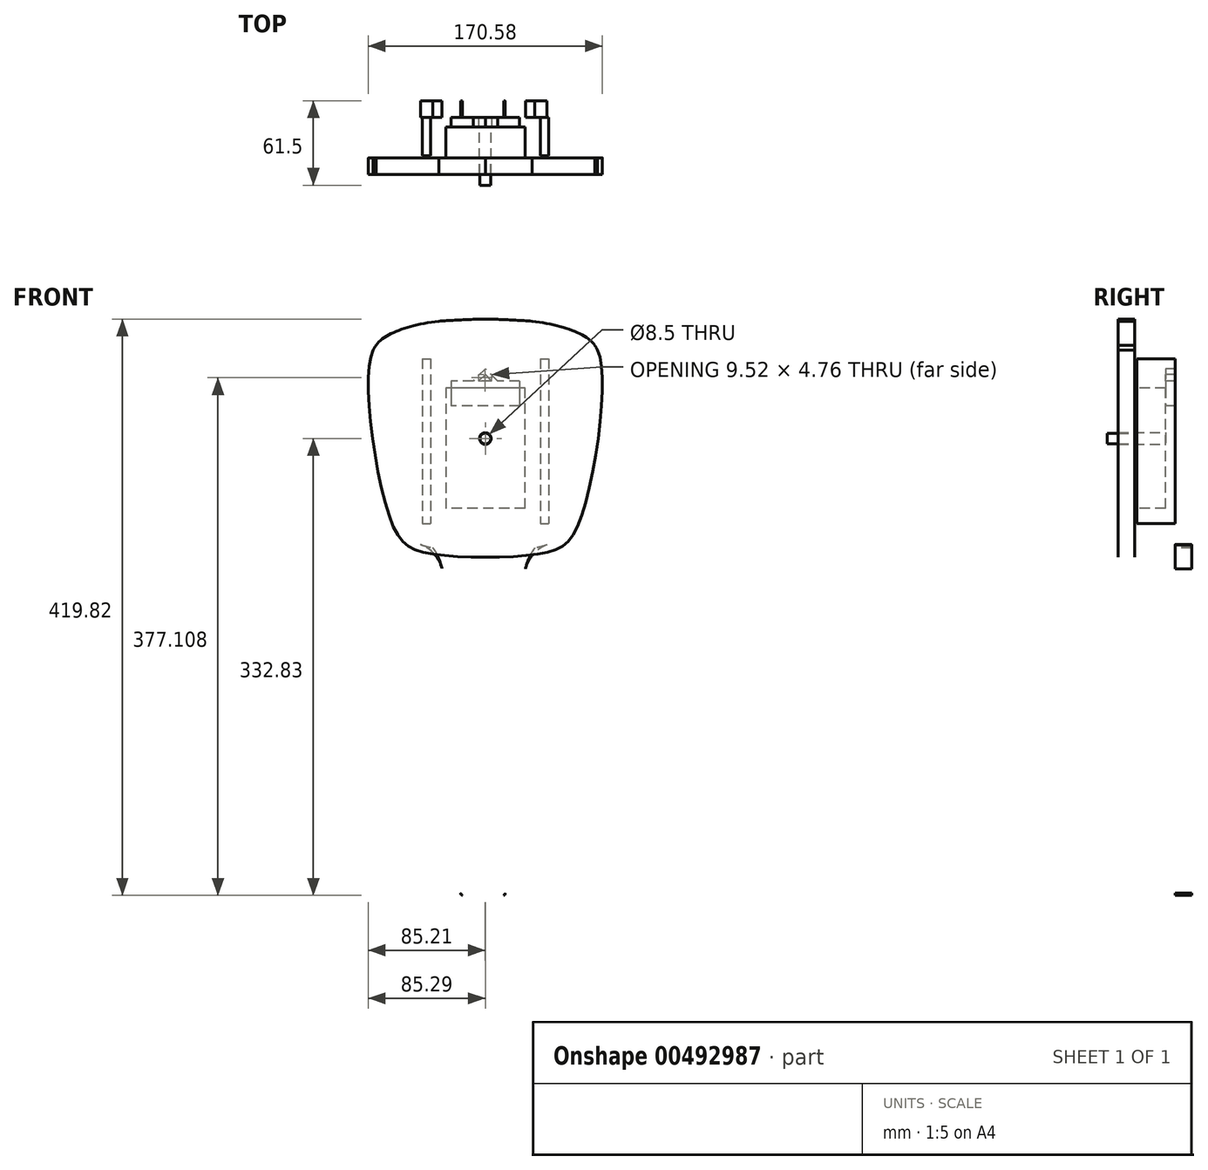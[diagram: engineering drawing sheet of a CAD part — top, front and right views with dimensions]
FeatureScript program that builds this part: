
annotation { "Feature Type Name" : "Feature", "Feature Type Description" : "" }
export const myFeature = defineFeature(function(context is Context, id is Id, definition is map)
    precondition{}
    {
        {
            var Q0;
            Q0=qCreatedBy(makeId("Front.planeOp"),FACE);
            var sketch = newSketch(context, id + "F0", { "sketchPlane" : qUnion([Q0])});
            skLineSegment(sketch, "E0", {"start": v(0, 92.19) * mm, "end": v(0, -94.4) * mm, "construction": true});
            skFitSpline(sketch, "E1", {"points": [v(-34.18, 85.43) * mm, v(-82.75, 62.27) * mm, v(-69.15, -63.66) * mm, v(-45.13, -83.34) * mm, v(40.74, -83.8) * mm, v(67.58, -62.92) * mm, v(84.8, 51.66) * mm, v(72.84, 74.07) * mm, v(35.33, 85.27) * mm, v(-34.18, 85.43) * mm]});
            skFitSpline(sketch, "E2.MirrorCS", {"points": [v(34.18, 85.43) * mm, v(82.75, 62.27) * mm, v(69.15, -63.66) * mm, v(45.13, -83.34) * mm, v(-40.74, -83.8) * mm, v(-67.58, -62.92) * mm, v(-84.8, 51.66) * mm, v(-72.84, 74.07) * mm, v(-35.33, 85.27) * mm, v(34.18, 85.43) * mm]});
            skSolve(sketch);
        }
        {
            var Q0;
            Q0=makeQuery(id+"F0.imprint","IMPRINT",FACE,{"disambiguationData":[TD([[makeQuery(id+"F0.imprint","IMPRINT",EDGE,{"derivedFrom":sQuery(id+"F0.wireOp",EDGE,"E1")}),1.0]])]});
            extrude(context, id + "F1", {"entities" : qUnion([Q0]), "depth" : 12 * mm});
        }
        {
            var Q0;
            Q0=makeQuery(id+"F1.opExtrude","CAP_FACE",FACE,{"disambiguationData":[OSD([sQuery(id+"F0.wireOp",EDGE,"E1"),sQuery(id+"F0.wireOp",EDGE,"E2.MirrorCS")])],"isStart":true});
            var sketch = newSketch(context, id + "F2", { "sketchPlane" : qUnion([Q0])});
            skCircle(sketch, "E3", {"center": v(0, 0) * mm, "radius": 4.25 * mm});
            skSolve(sketch);
        }
        {
            var Q0;
            Q0=makeQuery(id+"F2.imprint","IMPRINT",FACE,{"disambiguationData":[TD([[makeQuery(id+"F2.imprint","IMPRINT",EDGE,{"derivedFrom":sQuery(id+"F2.wireOp",EDGE,"E3")}),1.0]])]});
            extrude(context, id + "F3", {"entities" : qUnion([Q0]), "operationType" : NewBodyOperationType.REMOVE, "oppositeDirection" : true, "depth" : 25 * mm});
        }
        {
            var Q0;
            Q0=makeQuery(id+"F1.opExtrude","CAP_FACE",FACE,{"disambiguationData":[OSD([sQuery(id+"F0.wireOp",EDGE,"E1"),sQuery(id+"F0.wireOp",EDGE,"E2.MirrorCS")])],"isStart":false});
            var sketch = newSketch(context, id + "F4", { "sketchPlane" : qUnion([Q0])});
            skCircle(sketch, "E4", {"center": v(0, 0) * mm, "radius": 3.9 * mm});
            skSolve(sketch);
        }
        {
            var Q0;
            Q0=makeQuery(id+"F4.imprint","IMPRINT",FACE,{"disambiguationData":[TD([[makeQuery(id+"F4.imprint","IMPRINT",EDGE,{"derivedFrom":sQuery(id+"F4.wireOp",EDGE,"E4")}),1.0]])]});
            var Q1;
            Q1=sQuery(id+"F4.wireOp",EDGE,"E4");
            extrude(context, id + "F5", {"entities" : qUnion([Q0]), "surfaceEntities" : qUnion([Q1]), "depth" : 8 * mm, "hasSecondDirection" : true, "secondDirectionOppositeDirection" : true, "secondDirectionDepth" : 12 * mm});
        }
        {
            var Q0;
            Q0=makeQuery(id+"F1.opExtrude","CAP_FACE",FACE,{"disambiguationData":[OSD([sQuery(id+"F0.wireOp",EDGE,"E1"),sQuery(id+"F0.wireOp",EDGE,"E2.MirrorCS")])],"isStart":true});
            var sketch = newSketch(context, id + "F6", { "sketchPlane" : qUnion([Q0])});
            skLineSegment(sketch, "E5", {"start": v(-28.9, 36.9) * mm, "end": v(28.9, 36.9) * mm});
            skLineSegment(sketch, "E6", {"start": v(-28.9, -50.9) * mm, "end": v(28.9, -50.9) * mm});
            skLineSegment(sketch, "E7", {"start": v(-28.9, -50.9) * mm, "end": v(-28.9, 36.9) * mm});
            skLineSegment(sketch, "E8", {"start": v(28.9, 36.9) * mm, "end": v(28.9, -50.9) * mm});
            skSolve(sketch);
        }
        {
            var Q0;
            Q0=makeQuery(id+"F6.imprint","IMPRINT",FACE,{"disambiguationData":[TD([[makeQuery(id+"F6.imprint","IMPRINT",EDGE,{"derivedFrom":sQuery(id+"F6.wireOp",EDGE,"E5")}),-1.0]])]});
            extrude(context, id + "F7", {"entities" : qUnion([Q0]), "operationType" : NewBodyOperationType.ADD, "depth" : 22.5 * mm});
        }
        {
            var Q0;
            Q0=makeQuery(id+"F7.opExtrude","CAP_FACE",FACE,{"disambiguationData":[OSD([sQuery(id+"F2.wireOp",EDGE,"E3"),sQuery(id+"F6.wireOp",EDGE,"E5"),sQuery(id+"F6.wireOp",EDGE,"E6"),sQuery(id+"F6.wireOp",EDGE,"E7"),sQuery(id+"F6.wireOp",EDGE,"E8")])],"isStart":false});
            var sketch = newSketch(context, id + "F8", { "sketchPlane" : qUnion([Q0])});
            skLineSegment(sketch, "E9.bottom", {"start": v(-25, 41.9) * mm, "end": v(-8.85, 41.9) * mm});
            skLineSegment(sketch, "E9.top", {"start": v(-25, 23.9) * mm, "end": v(25, 23.9) * mm});
            skLineSegment(sketch, "E9.left", {"start": v(-25, 41.9) * mm, "end": v(-25, 23.9) * mm});
            skLineSegment(sketch, "E9.right", {"start": v(25, 41.9) * mm, "end": v(25, 23.9) * mm});
            skLineSegment(sketch, "E10", {"start": v(-8.85, 41.9) * mm, "end": v(0, 50.9) * mm});
            skPoint(sketch, "E10.endSnap0", {"position": v(0, 41.9) * mm});
            skLineSegment(sketch, "E11", {"start": v(0, 50.9) * mm, "end": v(8.85, 41.9) * mm});
            skLineSegment(sketch, "E12", {"start": v(-4.68, 41.9) * mm, "end": v(0, 46.66) * mm});
            skLineSegment(sketch, "E13", {"start": v(0, 46.66) * mm, "end": v(4.84, 41.9) * mm});
            skLineSegment(sketch, "E14.trimOffspring", {"start": v(-4.68, 41.9) * mm, "end": v(4.84, 41.9) * mm});
            skLineSegment(sketch, "E15.trimOffspring", {"start": v(8.85, 41.9) * mm, "end": v(25, 41.9) * mm});
            skSolve(sketch);
        }
        {
            var Q0;
            Q0 = qSketchRegion(id + "F8", true);
            extrude(context, id + "F9", {"entities" : qUnion([Q0]), "operationType" : NewBodyOperationType.ADD, "depth" : 7 * mm});
        }
        {
            var Q0;
            Q0=makeQuery(id+"F9.opExtrude","CAP_FACE",FACE,{"disambiguationData":[OSD([sQuery(id+"F8.wireOp",EDGE,"E9.bottom"),sQuery(id+"F8.wireOp",EDGE,"E9.top"),sQuery(id+"F8.wireOp",EDGE,"E9.left"),sQuery(id+"F8.wireOp",EDGE,"E9.right"),sQuery(id+"F8.wireOp",EDGE,"E10"),sQuery(id+"F8.wireOp",EDGE,"E11"),sQuery(id+"F8.wireOp",EDGE,"E12"),sQuery(id+"F8.wireOp",EDGE,"E13"),sQuery(id+"F8.wireOp",EDGE,"E14.trimOffspring"),sQuery(id+"F8.wireOp",EDGE,"E15.trimOffspring")])],"isStart":false});
            var sketch = newSketch(context, id + "F10", { "sketchPlane" : qUnion([Q0])});
            skLineSegment(sketch, "E16", {"start": v(0.68, 132.03) * mm, "end": v(1.75, -338.07) * mm, "construction": true});
            skFitSpline(sketch, "E17.MirrorCS", {"points": [v(-36.07, -79.67) * mm, v(-38.31, -176.64) * mm], "startDerivative": vector(50.2, -64.86) * mm, "endDerivative": vector(-28.7, -66.43) * mm});
            skFitSpline(sketch, "E18.MirrorCS", {"points": [v(-39.85, -215.04) * mm, v(-38.31, -176.64) * mm], "startDerivative": vector(31.7, 21.38) * mm, "endDerivative": vector(-33.38, 61.08) * mm});
            skFitSpline(sketch, "E19.MirrorCS", {"points": [v(-36.04, -307.45) * mm, v(-49.96, -244.84) * mm, v(-39.85, -215.04) * mm], "startDerivative": vector(-116.27, 61.82) * mm, "endDerivative": vector(-62.13, 120.79) * mm});
            skFitSpline(sketch, "E20.MirrorCS", {"points": [v(-14.34, -332.34) * mm, v(-36.04, -307.45) * mm], "startDerivative": vector(-3.75, 31.65) * mm, "endDerivative": vector(-77.3, 0.44) * mm});
            skFitSpline(sketch, "E21.MirrorCS", {"points": [v(1.75, -336.2) * mm, v(-14.34, -332.34) * mm], "startDerivative": vector(-19.67, 0.05) * mm, "endDerivative": vector(-18.57, 8.9) * mm});
            skFitSpline(sketch, "E22.MirrorCS", {"points": [v(0.68, 129.14) * mm, v(-27.26, 114.23) * mm, v(-34.7, 85) * mm], "startDerivative": vector(-112.99, -1.75) * mm, "endDerivative": vector(-93.9, -67.91) * mm});
            skFitSpline(sketch, "E23.0", {"points": [v(31.63, 66.56) * mm, v(32.75, 66.48) * mm, v(33.87, 66.4) * mm, v(35.34, 66.28) * mm, v(37.14, 66.13) * mm, v(39.25, 65.94) * mm, v(41.97, 65.66) * mm, v(45.2, 65.27) * mm, v(48.76, 64.7) * mm, v(51.96, 64.05) * mm, v(54.77, 63.28) * mm, v(57.15, 62.44) * mm, v(59.1, 61.54) * mm, v(60.67, 60.62) * mm, v(61.9, 59.67) * mm, v(62.95, 58.65) * mm, v(63.75, 57.63) * mm, v(64.37, 56.63) * mm, v(64.76, 55.92) * mm, v(65.07, 55.27) * mm, v(65.3, 54.76) * mm, v(65.53, 54.19) * mm, v(65.85, 53.35) * mm, v(66.24, 52.17) * mm, v(66.84, 50) * mm, v(67.51, 46.8) * mm, v(68.13, 42.3) * mm, v(68.66, 35.57) * mm, v(68.72, 26) * mm, v(67.9, 13.36) * mm, v(66.26, 0.16) * mm, v(63.99, -13.1) * mm, v(61.22, -25.87) * mm, v(58.65, -35.7) * mm, v(56.53, -42.8) * mm, v(54.94, -47.69) * mm, v(53.64, -51.3) * mm, v(52.64, -53.9) * mm, v(51.92, -55.66) * mm, v(51.23, -57.24) * mm, v(50.38, -59.05) * mm, v(49.46, -60.8) * mm, v(48.62, -62.1) * mm, v(48.12, -62.7) * mm, v(47.92, -62.87) * mm, v(47.86, -62.92) * mm, v(47.6, -63.08) * mm, v(46.8, -63.42) * mm, v(45.29, -63.9) * mm, v(43.55, -64.3) * mm, v(42.15, -64.57) * mm, v(41.14, -64.76) * mm, v(39.26, -65.08) * mm, v(36.22, -65.52) * mm, v(32.14, -66) * mm, v(27.68, -66.43) * mm, v(22.92, -66.78) * mm, v(16.27, -67.17) * mm, v(7.5, -67.47) * mm, v(-3.27, -67.53) * mm, v(-13.85, -67.28) * mm, v(-22.14, -66.82) * mm, v(-28.2, -66.3) * mm, v(-32.4, -65.83) * mm, v(-35.54, -65.4) * mm, v(-37.8, -65.02) * mm, v(-39.32, -64.74) * mm, v(-40.67, -64.46) * mm, v(-42.24, -64.08) * mm, v(-43.76, -63.63) * mm, v(-44.93, -63.15) * mm, v(-45.6, -62.8) * mm, v(-45.97, -62.53) * mm, v(-46.32, -62.22) * mm, v(-46.86, -61.61) * mm, v(-47.65, -60.5) * mm, v(-48.66, -58.7) * mm, v(-49.85, -56.14) * mm, v(-51.18, -52.8) * mm, v(-53.03, -47.48) * mm, v(-55.38, -39.45) * mm, v(-58.06, -28.26) * mm, v(-60.49, -16.06) * mm, v(-62.59, -3.35) * mm, v(-64.28, 9.4) * mm, v(-65.52, 21.7) * mm, v(-66.1, 31.15) * mm, v(-66.3, 37.97) * mm, v(-66.3, 42.62) * mm, v(-66.18, 46.04) * mm, v(-66.02, 48.44) * mm, v(-65.87, 50.05) * mm, v(-65.7, 51.47) * mm, v(-65.46, 53.11) * mm, v(-65.12, 54.7) * mm, v(-64.75, 55.9) * mm, v(-64.48, 56.52) * mm, v(-64.35, 56.73) * mm, v(-64.3, 56.78) * mm, v(-64.2, 56.9) * mm, v(-63.89, 57.18) * mm, v(-63.42, 57.53) * mm, v(-63.02, 57.8) * mm, v(-62.64, 58.04) * mm, v(-62.23, 58.29) * mm, v(-61.67, 58.61) * mm, v(-60.92, 59.02) * mm, v(-59.82, 59.57) * mm, v(-57.66, 60.57) * mm, v(-53.9, 62) * mm, v(-48.5, 63.59) * mm, v(-42.31, 64.99) * mm, v(-36.62, 65.95) * mm, v(-31.8, 66.58) * mm, v(-26.8, 67.11) * mm, v(-20.2, 67.61) * mm, v(-11.88, 67.95) * mm, v(-3.23, 68.05) * mm, v(4.16, 67.95) * mm, v(10.15, 67.77) * mm, v(14.66, 67.59) * mm, v(19.2, 67.37) * mm, v(22.97, 67.15) * mm, v(25.99, 66.96) * mm, v(28.24, 66.8) * mm, v(30.12, 66.67) * mm, v(31.63, 66.56) * mm, v(32.75, 66.48) * mm, v(33.87, 66.4) * mm]});
            skFitSpline(sketch, "E24", {"points": [v(-34.7, 85) * mm, v(-64.67, 56.06) * mm], "startDerivative": vector(-40, -29.15) * mm, "endDerivative": vector(-19.35, -43.23) * mm});
            skFitSpline(sketch, "E25.trimOffspring", {"points": [v(-31.75, 68.26) * mm, v(-32.88, 68.18) * mm, v(-34, 68.09) * mm, v(-35.48, 67.97) * mm, v(-37.3, 67.82) * mm, v(-39.41, 67.63) * mm, v(-42.16, 67.35) * mm, v(-45.43, 66.96) * mm, v(-49.06, 66.38) * mm, v(-52.35, 65.7) * mm, v(-55.27, 64.91) * mm, v(-57.78, 64.02) * mm, v(-59.89, 63.06) * mm, v(-61.6, 62.04) * mm, v(-63.02, 60.96) * mm, v(-64.22, 59.78) * mm, v(-65.14, 58.61) * mm, v(-65.84, 57.5) * mm, v(-66.28, 56.7) * mm, v(-66.62, 55.99) * mm, v(-66.87, 55.42) * mm, v(-67.12, 54.8) * mm, v(-67.45, 53.91) * mm, v(-67.87, 52.66) * mm, v(-68.5, 50.4) * mm, v(-69.2, 47.09) * mm, v(-69.82, 42.48) * mm, v(-70.36, 35.62) * mm, v(-70.42, 25.94) * mm, v(-69.58, 13.2) * mm, v(-67.95, -0.1) * mm, v(-65.66, -13.41) * mm, v(-62.88, -26.26) * mm, v(-60.29, -36.15) * mm, v(-58.16, -43.31) * mm, v(-56.55, -48.23) * mm, v(-55.24, -51.9) * mm, v(-54.22, -54.52) * mm, v(-53.48, -56.32) * mm, v(-52.78, -57.93) * mm, v(-51.9, -59.8) * mm, v(-50.94, -61.64) * mm, v(-50.02, -63.07) * mm, v(-49.39, -63.83) * mm, v(-49.03, -64.17) * mm, v(-48.78, -64.36) * mm, v(-48.33, -64.62) * mm, v(-47.37, -65.03) * mm, v(-45.71, -65.54) * mm, v(-43.9, -65.96) * mm, v(-42.46, -66.24) * mm, v(-41.44, -66.43) * mm, v(-39.52, -66.76) * mm, v(-36.44, -67.2) * mm, v(-32.31, -67.7) * mm, v(-27.82, -68.12) * mm, v(-23.04, -68.48) * mm, v(-16.34, -68.87) * mm, v(-7.54, -69.17) * mm, v(3.28, -69.23) * mm, v(13.92, -68.98) * mm, v(22.26, -68.51) * mm, v(28.37, -67.98) * mm, v(32.61, -67.52) * mm, v(35.8, -67.08) * mm, v(38.09, -66.7) * mm, v(39.65, -66.41) * mm, v(41.04, -66.12) * mm, v(42.68, -65.73) * mm, v(44.3, -65.24) * mm, v(45.63, -64.7) * mm, v(46.47, -64.26) * mm, v(47.02, -63.87) * mm, v(47.55, -63.4) * mm, v(48.22, -62.64) * mm, v(49.1, -61.38) * mm, v(50.18, -59.46) * mm, v(51.41, -56.8) * mm, v(52.77, -53.4) * mm, v(54.65, -47.99) * mm, v(57.02, -39.88) * mm, v(59.72, -28.62) * mm, v(62.16, -16.36) * mm, v(64.27, -3.6) * mm, v(65.97, 9.2) * mm, v(67.21, 21.55) * mm, v(67.8, 31.07) * mm, v(68, 37.94) * mm, v(68, 42.65) * mm, v(67.87, 46.12) * mm, v(67.71, 48.57) * mm, v(67.56, 50.23) * mm, v(67.39, 51.7) * mm, v(67.13, 53.41) * mm, v(66.77, 55.1) * mm, v(66.35, 56.47) * mm, v(66.01, 57.26) * mm, v(65.78, 57.65) * mm, v(65.62, 57.87) * mm, v(65.37, 58.14) * mm, v(64.94, 58.52) * mm, v(64.4, 58.92) * mm, v(63.95, 59.22) * mm, v(63.54, 59.48) * mm, v(63.1, 59.75) * mm, v(62.5, 60.1) * mm, v(61.7, 60.53) * mm, v(60.56, 61.1) * mm, v(58.3, 62.14) * mm, v(54.44, 63.61) * mm, v(48.92, 65.24) * mm, v(42.64, 66.66) * mm, v(36.87, 67.63) * mm, v(32, 68.27) * mm, v(26.94, 68.8) * mm, v(20.3, 69.31) * mm, v(11.92, 69.65) * mm, v(3.23, 69.75) * mm, v(-4.2, 69.65) * mm, v(-10.21, 69.47) * mm, v(-14.74, 69.29) * mm, v(-19.28, 69.06) * mm, v(-23.07, 68.85) * mm, v(-26.1, 68.65) * mm, v(-28.36, 68.5) * mm, v(-30.25, 68.37) * mm, v(-31.75, 68.26) * mm, v(-32.88, 68.18) * mm, v(-34, 68.09) * mm]});
            skLineSegment(sketch, "E26", {"start": v(-65.9, 28.06) * mm, "end": v(-60.45, -63.33) * mm});
            skFitSpline(sketch, "E27", {"points": [v(-60.45, -63.33) * mm, v(-36.07, -79.67) * mm], "startDerivative": vector(2.68, -21.93) * mm, "endDerivative": vector(36.37, -4.78) * mm});
            skPoint(sketch, "E28.start.orphan", {"position": v(-46.74, -61.74) * mm});
            skArc(sketch, "E29.filletArc", {"start": v(-29.19, -94.95) * mm, "mid": v(-34.82, -84.29) * mm, "end": v(-44.8, -77.5) * mm});
            skArc(sketch, "E30.filletArc", {"start": v(-14.45, -331.17) * mm, "mid": v(-14.1, -332.15) * mm, "end": v(-13.3, -332.83) * mm});
            skFitSpline(sketch, "E31.MirrorCS", {"points": [v(0.68, 129.14) * mm, v(28.7, 114.35) * mm, v(36.27, 85.15) * mm], "startDerivative": vector(113, -1.24) * mm, "endDerivative": vector(94.2, -67.48) * mm});
            skFitSpline(sketch, "E32.MirrorCS", {"points": [v(36.27, 85.15) * mm, v(66.37, 56.36) * mm], "startDerivative": vector(40.12, -28.96) * mm, "endDerivative": vector(19.55, -43.14) * mm});
            skLineSegment(sketch, "E33.MirrorCS", {"start": v(67.72, 28.37) * mm, "end": v(62.7, -63.05) * mm});
            skFitSpline(sketch, "E34.MirrorCS", {"points": [v(62.7, -63.05) * mm, v(38.39, -79.5) * mm], "startDerivative": vector(-2.58, -21.94) * mm, "endDerivative": vector(-36.35, -4.95) * mm});
            skArc(sketch, "E35.MirrorCS", {"start": v(31.58, -94.81) * mm, "mid": v(37.17, -84.12) * mm, "end": v(47.1, -77.3) * mm});
            skFitSpline(sketch, "E36.MirrorCS", {"points": [v(38.39, -79.5) * mm, v(41.08, -176.46) * mm], "startDerivative": vector(-49.9, -65.09) * mm, "endDerivative": vector(29, -66.3) * mm});
            skFitSpline(sketch, "E37.MirrorCS", {"points": [v(42.8, -214.85) * mm, v(41.08, -176.46) * mm], "startDerivative": vector(-31.8, 21.23) * mm, "endDerivative": vector(33.1, 61.23) * mm});
            skFitSpline(sketch, "E38.MirrorCS", {"points": [v(39.4, -307.28) * mm, v(53.04, -244.6) * mm, v(42.8, -214.85) * mm], "startDerivative": vector(115.98, 62.35) * mm, "endDerivative": vector(61.58, 121.07) * mm});
            skFitSpline(sketch, "E39.MirrorCS", {"points": [v(17.81, -332.26) * mm, v(39.4, -307.28) * mm], "startDerivative": vector(3.6, 31.66) * mm, "endDerivative": vector(77.3, 0.79) * mm});
            skFitSpline(sketch, "E40.MirrorCS", {"points": [v(1.75, -336.2) * mm, v(17.81, -332.26) * mm], "startDerivative": vector(19.67, 0.14) * mm, "endDerivative": vector(18.53, 8.99) * mm});
            skArc(sketch, "E41.MirrorCS", {"start": v(17.92, -331.1) * mm, "mid": v(17.57, -332.08) * mm, "end": v(16.78, -332.76) * mm});
            skFitSpline(sketch, "E42", {"points": [v(66.37, 56.36) * mm, v(67.72, 28.37) * mm], "startDerivative": vector(9.01, -18.35) * mm, "endDerivative": vector(-0.92, -26.47) * mm});
            skSolve(sketch);
        }
        {
            var Q0;
            Q0 = qSketchRegion(id + "F10", true);
            extrude(context, id + "F11", {"entities" : qUnion([Q0]), "depth" : 12 * mm});
        }
        {
            var Q0;
            Q0=makeQuery(id+"F11.opExtrude","CAP_FACE",FACE,{"disambiguationData":[OSD([sQuery(id+"F10.wireOp",EDGE,"E17.MirrorCS"),sQuery(id+"F10.wireOp",EDGE,"E18.MirrorCS"),sQuery(id+"F10.wireOp",EDGE,"E19.MirrorCS"),sQuery(id+"F10.wireOp",EDGE,"E20.MirrorCS"),sQuery(id+"F10.wireOp",EDGE,"E21.MirrorCS"),sQuery(id+"F10.wireOp",EDGE,"E22.MirrorCS"),sQuery(id+"F10.wireOp",EDGE,"E23.0"),sQuery(id+"F10.wireOp",EDGE,"E24"),sQuery(id+"F10.wireOp",EDGE,"E26"),sQuery(id+"F10.wireOp",EDGE,"E27"),sQuery(id+"F10.wireOp",EDGE,"E29.filletArc"),sQuery(id+"F10.wireOp",EDGE,"E30.filletArc"),sQuery(id+"F10.wireOp",EDGE,"E31.MirrorCS"),sQuery(id+"F10.wireOp",EDGE,"E32.MirrorCS"),sQuery(id+"F10.wireOp",EDGE,"E33.MirrorCS"),sQuery(id+"F10.wireOp",EDGE,"E34.MirrorCS"),sQuery(id+"F10.wireOp",EDGE,"E35.MirrorCS"),sQuery(id+"F10.wireOp",EDGE,"E36.MirrorCS"),sQuery(id+"F10.wireOp",EDGE,"E37.MirrorCS"),sQuery(id+"F10.wireOp",EDGE,"E38.MirrorCS"),sQuery(id+"F10.wireOp",EDGE,"E39.MirrorCS"),sQuery(id+"F10.wireOp",EDGE,"E40.MirrorCS"),sQuery(id+"F10.wireOp",EDGE,"E41.MirrorCS"),sQuery(id+"F10.wireOp",EDGE,"E42")])],"isStart":true});
            var sketch = newSketch(context, id + "F12", { "sketchPlane" : qUnion([Q0])});
            skLineSegment(sketch, "E43.bottom", {"start": v(-46, 58.17) * mm, "end": v(-40, 58.17) * mm});
            skLineSegment(sketch, "E43.top", {"start": v(-46, -61.83) * mm, "end": v(-40, -61.83) * mm});
            skLineSegment(sketch, "E43.left", {"start": v(-46, 58.17) * mm, "end": v(-46, -61.83) * mm});
            skLineSegment(sketch, "E43.right", {"start": v(-40, 58.17) * mm, "end": v(-40, -61.83) * mm});
            skLineSegment(sketch, "E44.bottom", {"start": v(40, 58.17) * mm, "end": v(46, 58.17) * mm});
            skLineSegment(sketch, "E44.top", {"start": v(40, -61.83) * mm, "end": v(46, -61.83) * mm});
            skLineSegment(sketch, "E44.left", {"start": v(40, 58.17) * mm, "end": v(40, -61.83) * mm});
            skLineSegment(sketch, "E44.right", {"start": v(46, 58.17) * mm, "end": v(46, -61.83) * mm});
            skSolve(sketch);
        }
        {
            var Q0;
            Q0 = qSketchRegion(id + "F12", true);
            extrude(context, id + "F13", {"entities" : qUnion([Q0]), "depth" : 28 * mm});
        }
    });
